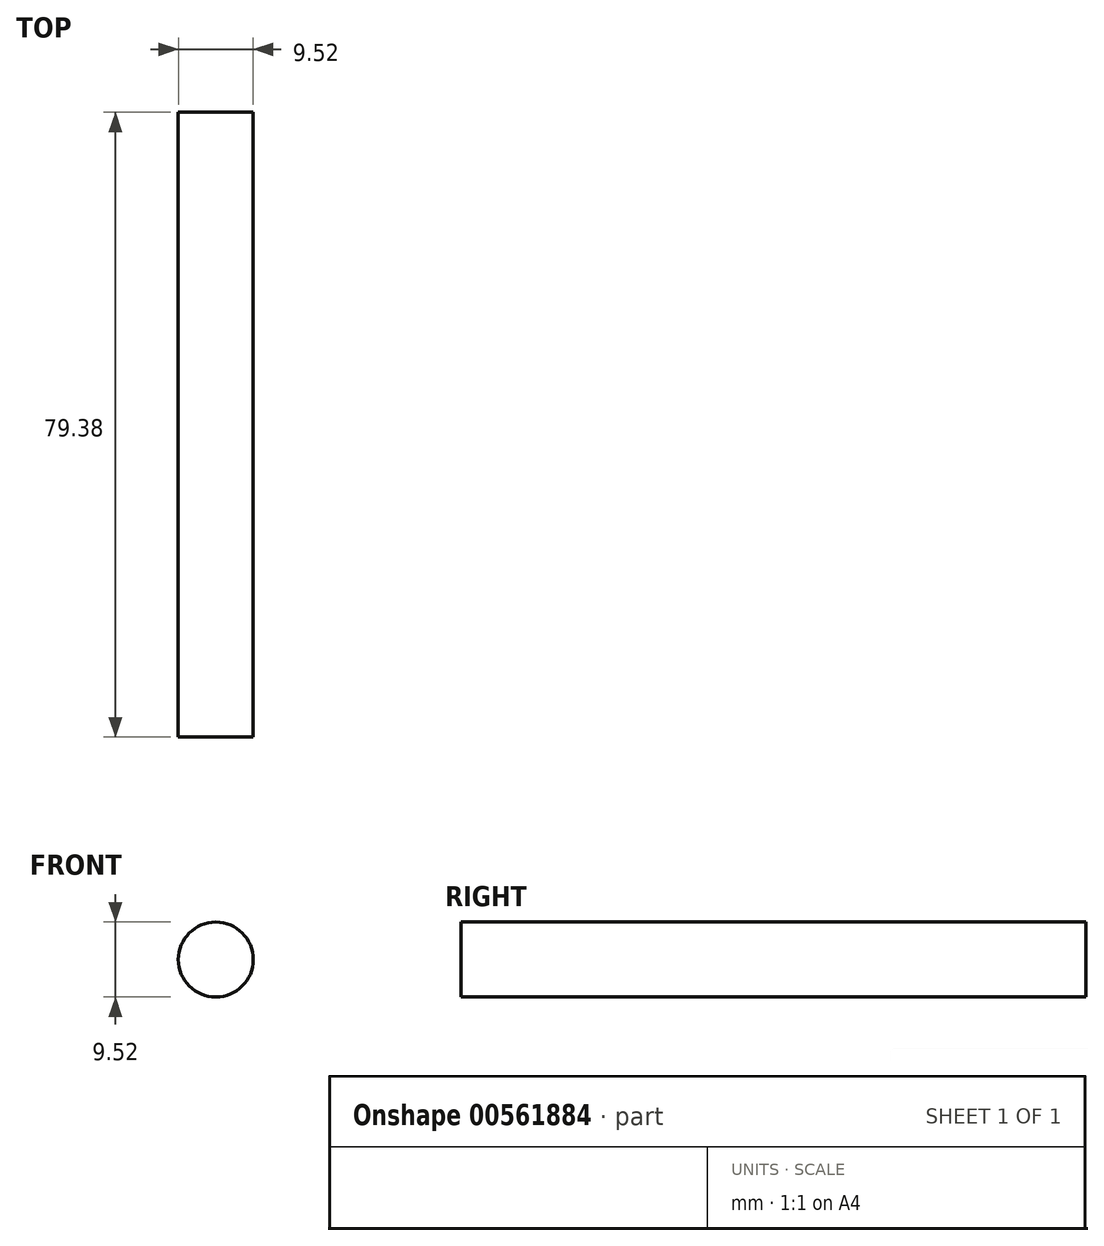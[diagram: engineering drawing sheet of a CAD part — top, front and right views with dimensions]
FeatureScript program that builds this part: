
annotation { "Feature Type Name" : "Feature", "Feature Type Description" : "" }
export const myFeature = defineFeature(function(context is Context, id is Id, definition is map)
    precondition{}
    {
        {
            var Q0;
            Q0=qCreatedBy(makeId("Front.planeOp"),FACE);
            var sketch = newSketch(context, id + "F0", { "sketchPlane" : qUnion([Q0])});
            skCircle(sketch, "E0", {"center": v(-35.91, 19.5) * mm, "radius": 4.76 * mm});
            skSolve(sketch);
        }
        {
            var Q0;
            Q0=makeQuery(id+"F0.imprint","IMPRINT",FACE,{"disambiguationData":[TD([[makeQuery(id+"F0.imprint","IMPRINT",EDGE,{"derivedFrom":sQuery(id+"F0.wireOp",EDGE,"E0")}),1.0]])]});
            extrude(context, id + "F1", {"entities" : qUnion([Q0]), "depth" : 79.38 * mm, "offsetDistance" : 25.4 * mm});
        }
    });
